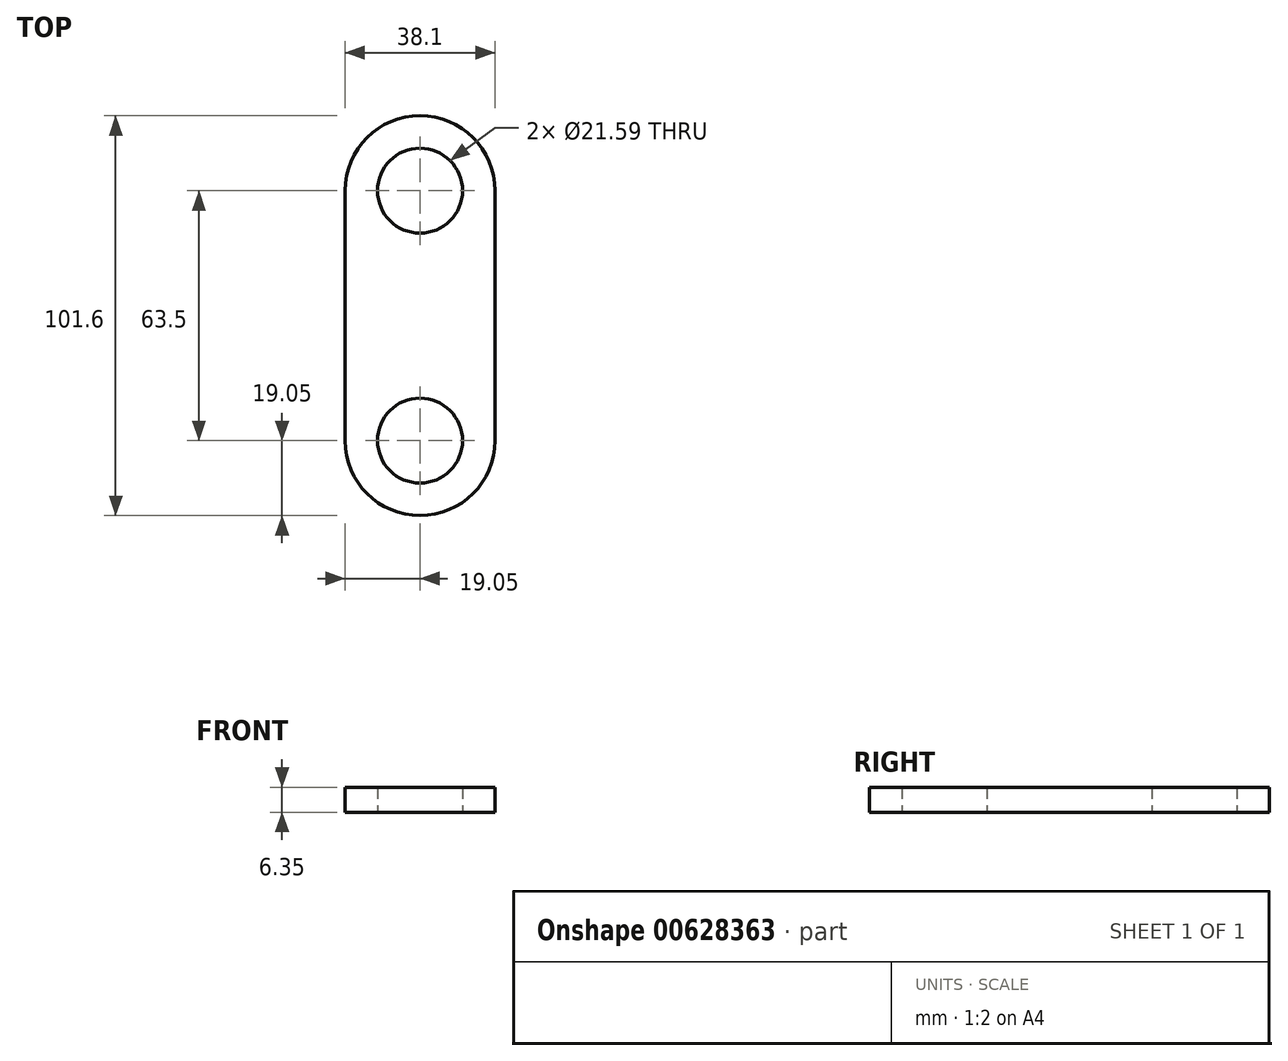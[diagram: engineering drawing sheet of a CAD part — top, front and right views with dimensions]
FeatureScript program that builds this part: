
annotation { "Feature Type Name" : "Feature", "Feature Type Description" : "" }
export const myFeature = defineFeature(function(context is Context, id is Id, definition is map)
    precondition{}
    {
        {
            var Q0;
            Q0=qCreatedBy(makeId("Top.planeOp"),FACE);
            var sketch = newSketch(context, id + "F0", { "sketchPlane" : qUnion([Q0])});
            skLineSegment(sketch, "E0", {"start": v(0, 0) * mm, "end": v(0, 69.2) * mm, "construction": true});
            skLineSegment(sketch, "E1", {"start": v(-19.05, 0) * mm, "end": v(-19.05, 63.5) * mm});
            skLineSegment(sketch, "E2.MirrorCS", {"start": v(19.05, 0) * mm, "end": v(19.05, 63.5) * mm});
            skArc(sketch, "E3", {"start": v(-19.05, 0) * mm, "mid": v(0, -19.05) * mm, "end": v(19.05, 0) * mm});
            skArc(sketch, "E4", {"start": v(-19.05, 63.5) * mm, "mid": v(0, 82.55) * mm, "end": v(19.05, 63.5) * mm});
            skCircle(sketch, "E5", {"center": v(0, 63.5) * mm, "radius": 10.8 * mm});
            skCircle(sketch, "E6", {"center": v(0, 0) * mm, "radius": 10.8 * mm});
            skSolve(sketch);
        }
        {
            var Q0;
            Q0 = qSketchRegion(id + "F0", true);
            extrude(context, id + "F1", {"entities" : qUnion([Q0]), "depth" : 6.35 * mm, "offsetDistance" : 25.4 * mm});
        }
    });
